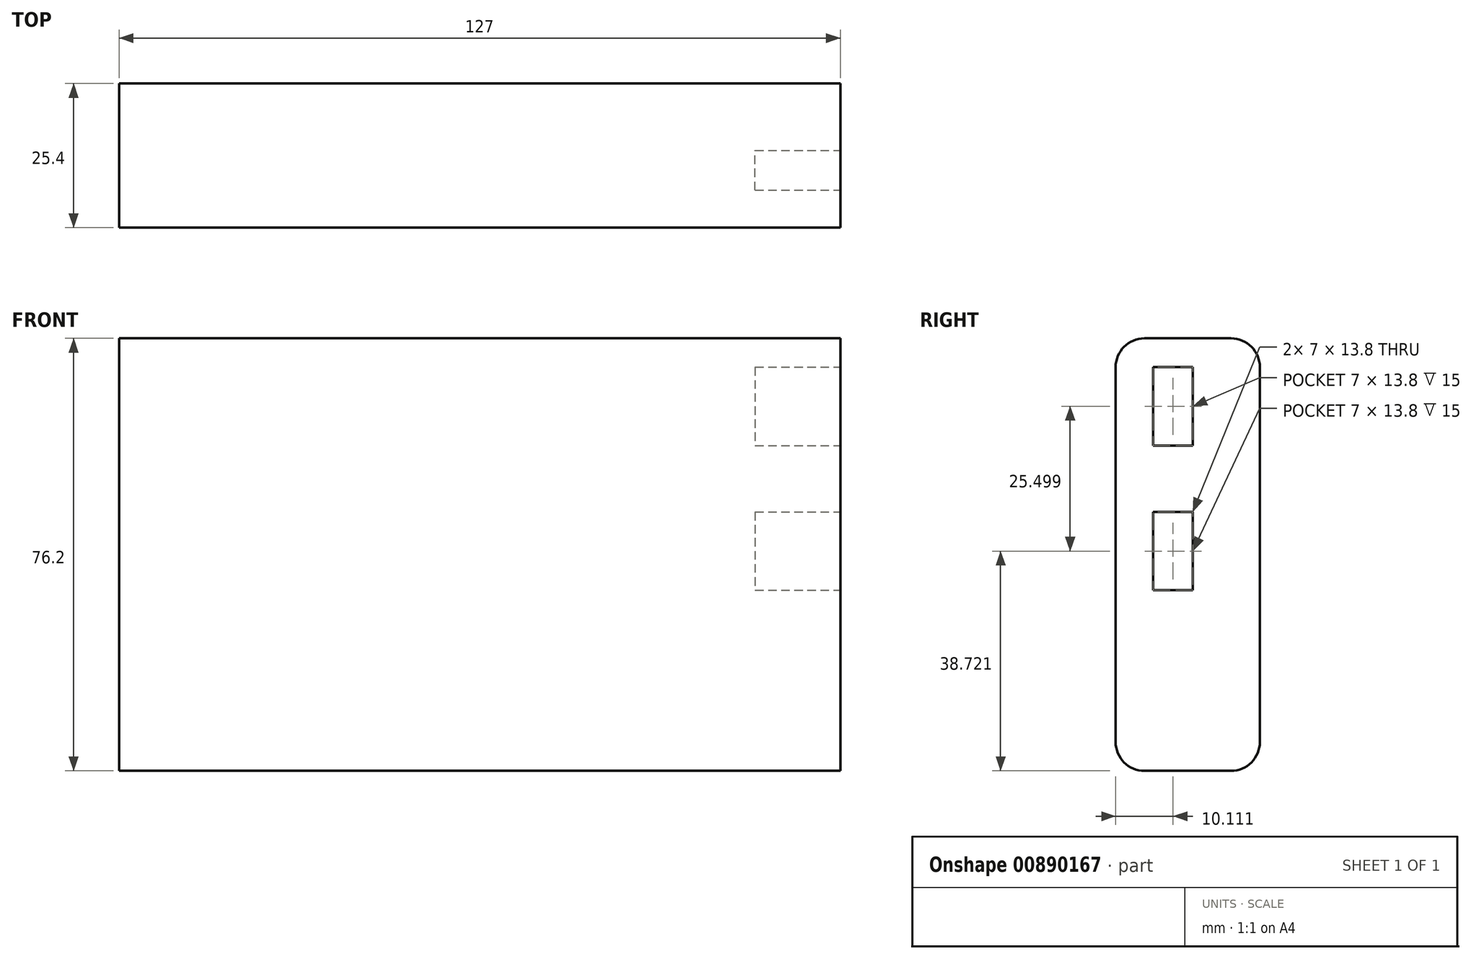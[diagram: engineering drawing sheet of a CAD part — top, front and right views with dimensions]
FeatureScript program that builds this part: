
annotation { "Feature Type Name" : "Feature", "Feature Type Description" : "" }
export const myFeature = defineFeature(function(context is Context, id is Id, definition is map)
    precondition{}
    {
        {
            var Q0;
            Q0=qCreatedBy(makeId("Front.planeOp"),FACE);
            var sketch = newSketch(context, id + "F0", { "sketchPlane" : qUnion([Q0])});
            skLineSegment(sketch, "E0.bottom", {"start": v(63.5, -38.1) * mm, "end": v(-63.5, -38.1) * mm});
            skLineSegment(sketch, "E0.top", {"start": v(63.5, 38.1) * mm, "end": v(-63.5, 38.1) * mm});
            skLineSegment(sketch, "E0.left", {"start": v(63.5, -38.1) * mm, "end": v(63.5, 38.1) * mm});
            skLineSegment(sketch, "E0.right", {"start": v(-63.5, -38.1) * mm, "end": v(-63.5, 38.1) * mm});
            skPoint(sketch, "E0.middle", {"position": v(0, 0) * mm});
            skSolve(sketch);
        }
        {
            var Q0;
            Q0 = qSketchRegion(id + "F0", true);
            extrude(context, id + "F1", {"entities" : qUnion([Q0]), "depth" : 25.4 * mm, "offsetDistance" : 25.4 * mm});
        }
        {
            var Q0;
            Q0=makeQuery(id+"F1.opExtrude","CAP_EDGE",EDGE,{"disambiguationData":[OSD([sQuery(id+"F0.wireOp",EDGE,"E0.top")])],"isStart":false});
            var Q1;
            Q1=makeQuery(id+"F1.opExtrude","CAP_EDGE",EDGE,{"disambiguationData":[OSD([sQuery(id+"F0.wireOp",EDGE,"E0.top")])],"isStart":true});
            var Q2;
            Q2=makeQuery(id+"F1.opExtrude","CAP_EDGE",EDGE,{"disambiguationData":[OSD([sQuery(id+"F0.wireOp",EDGE,"E0.bottom")])],"isStart":false});
            var Q3;
            Q3=makeQuery(id+"F1.opExtrude","CAP_EDGE",EDGE,{"disambiguationData":[OSD([sQuery(id+"F0.wireOp",EDGE,"E0.bottom")])],"isStart":true});
            fillet(context, id + "F2", {"entities" : qUnion([Q0, Q1, Q2, Q3]), "radius" : 5.08 * mm, "tangentPropagation" : true, "allowEdgeOverflow" : false});
        }
        {
            var Q0;
            Q0=makeQuery(id+"F1.opExtrude","SWEPT_FACE",FACE,{"disambiguationData":[OSD([sQuery(id+"F0.wireOp",EDGE,"E0.left")])]});
            var sketch = newSketch(context, id + "F3", { "sketchPlane" : qUnion([Q0])});
            skLineSegment(sketch, "E1.bottom", {"start": v(-18.79, 33.02) * mm, "end": v(-11.79, 33.02) * mm});
            skLineSegment(sketch, "E1.top", {"start": v(-18.79, 19.22) * mm, "end": v(-11.79, 19.22) * mm});
            skLineSegment(sketch, "E1.left", {"start": v(-18.79, 33.02) * mm, "end": v(-18.79, 19.22) * mm});
            skLineSegment(sketch, "E1.right", {"start": v(-11.79, 33.02) * mm, "end": v(-11.79, 19.22) * mm});
            skSolve(sketch);
        }
        {
            var Q0;
            Q0=makeQuery(id+"F3.imprint","IMPRINT",FACE,{"disambiguationData":[TD([[makeQuery(id+"F3.imprint","IMPRINT",EDGE,{"derivedFrom":sQuery(id+"F3.wireOp",EDGE,"E1.bottom")}),-1.0]])]});
            extrude(context, id + "F4", {"entities" : qUnion([Q0]), "operationType" : NewBodyOperationType.REMOVE, "oppositeDirection" : true, "depth" : 15 * mm, "offsetDistance" : 25.4 * mm});
        }
        {
            var Q0;
            Q0=makeQuery(id+"F1.opExtrude","SWEPT_FACE",FACE,{"disambiguationData":[OSD([sQuery(id+"F0.wireOp",EDGE,"E0.left")])]});
            var sketch = newSketch(context, id + "F5", { "sketchPlane" : qUnion([Q0])});
            skLineSegment(sketch, "E2.bottom", {"start": v(-18.79, 7.52) * mm, "end": v(-11.79, 7.52) * mm});
            skLineSegment(sketch, "E2.top", {"start": v(-18.79, -6.28) * mm, "end": v(-11.79, -6.28) * mm});
            skLineSegment(sketch, "E2.left", {"start": v(-18.79, 7.52) * mm, "end": v(-18.79, -6.28) * mm});
            skLineSegment(sketch, "E2.right", {"start": v(-11.79, 7.52) * mm, "end": v(-11.79, -6.28) * mm});
            skSolve(sketch);
        }
        {
            var Q0;
            Q0=makeQuery(id+"F5.imprint","IMPRINT",FACE,{"disambiguationData":[TD([[makeQuery(id+"F5.imprint","IMPRINT",EDGE,{"derivedFrom":sQuery(id+"F5.wireOp",EDGE,"E2.bottom")}),-1.0]])]});
            extrude(context, id + "F6", {"entities" : qUnion([Q0]), "operationType" : NewBodyOperationType.REMOVE, "oppositeDirection" : true, "depth" : 15 * mm, "offsetDistance" : 25.4 * mm});
        }
    });
